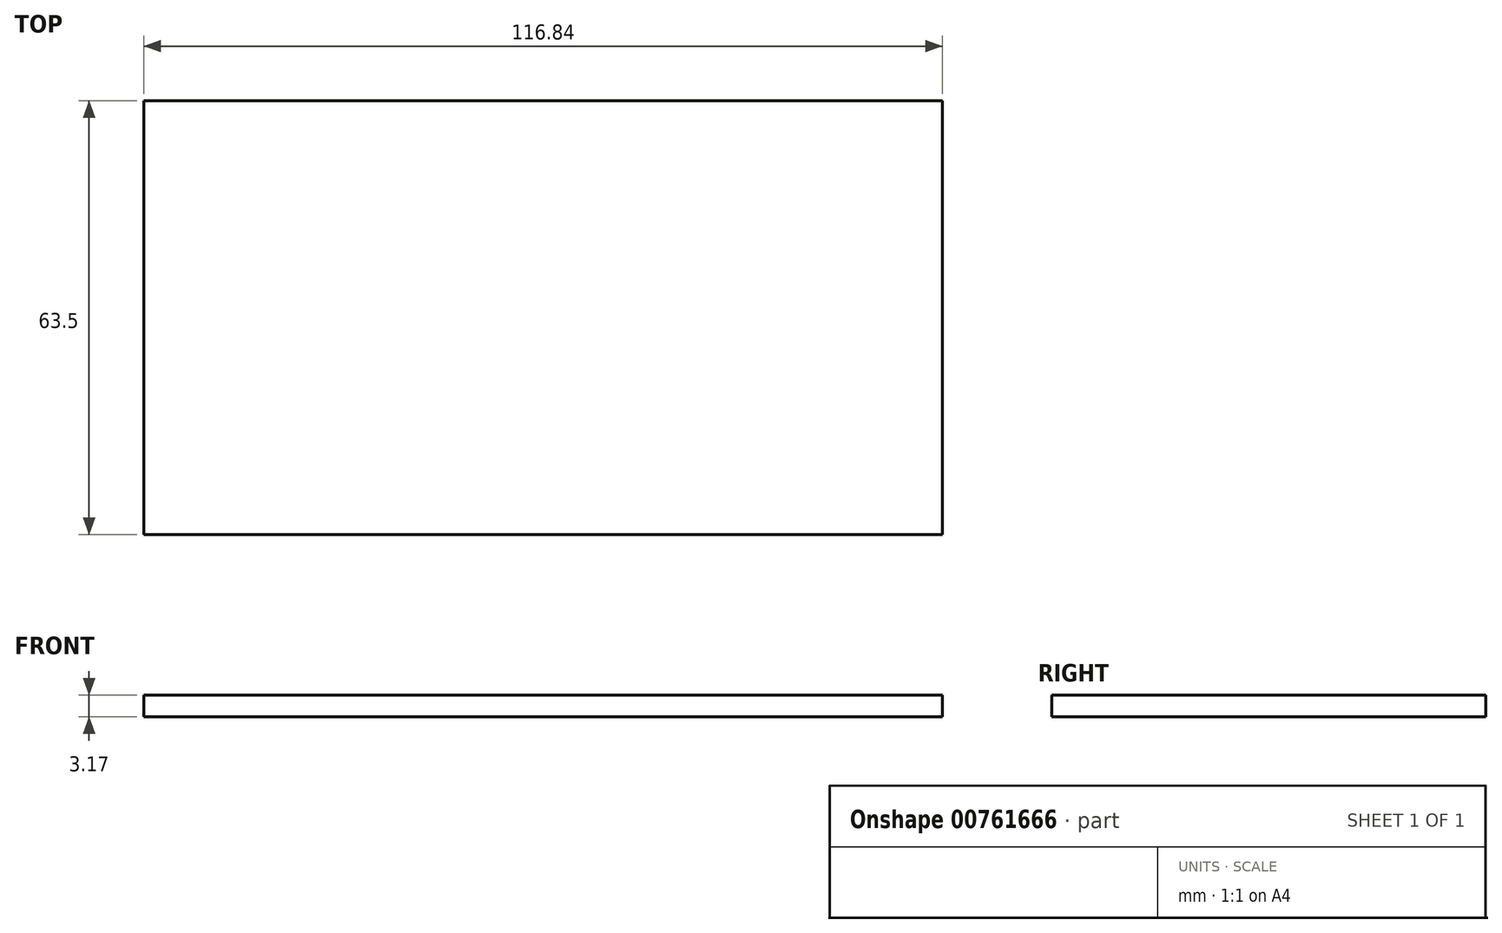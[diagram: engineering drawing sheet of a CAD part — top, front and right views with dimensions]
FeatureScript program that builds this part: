
annotation { "Feature Type Name" : "Feature", "Feature Type Description" : "" }
export const myFeature = defineFeature(function(context is Context, id is Id, definition is map)
    precondition{}
    {
        {
            var Q0;
            Q0=qCreatedBy(makeId("Top.planeOp"),FACE);
            var sketch = newSketch(context, id + "F0", { "sketchPlane" : qUnion([Q0])});
            skLineSegment(sketch, "E0.bottom", {"start": v(0, 0) * mm, "end": v(-116.84, 0) * mm});
            skLineSegment(sketch, "E0.top", {"start": v(0, 63.5) * mm, "end": v(-116.84, 63.5) * mm});
            skLineSegment(sketch, "E0.left", {"start": v(0, 0) * mm, "end": v(0, 63.5) * mm});
            skLineSegment(sketch, "E0.right", {"start": v(-116.84, 0) * mm, "end": v(-116.84, 63.5) * mm});
            skSolve(sketch);
        }
        {
            var Q0;
            Q0=makeQuery(id+"F0.imprint","IMPRINT",FACE,{"disambiguationData":[TD([[makeQuery(id+"F0.imprint","IMPRINT",EDGE,{"derivedFrom":sQuery(id+"F0.wireOp",EDGE,"E0.bottom")}),-1.0]])]});
            extrude(context, id + "F1", {"entities" : qUnion([Q0]), "depth" : 3.17 * mm, "offsetDistance" : 25.4 * mm});
        }
    });
